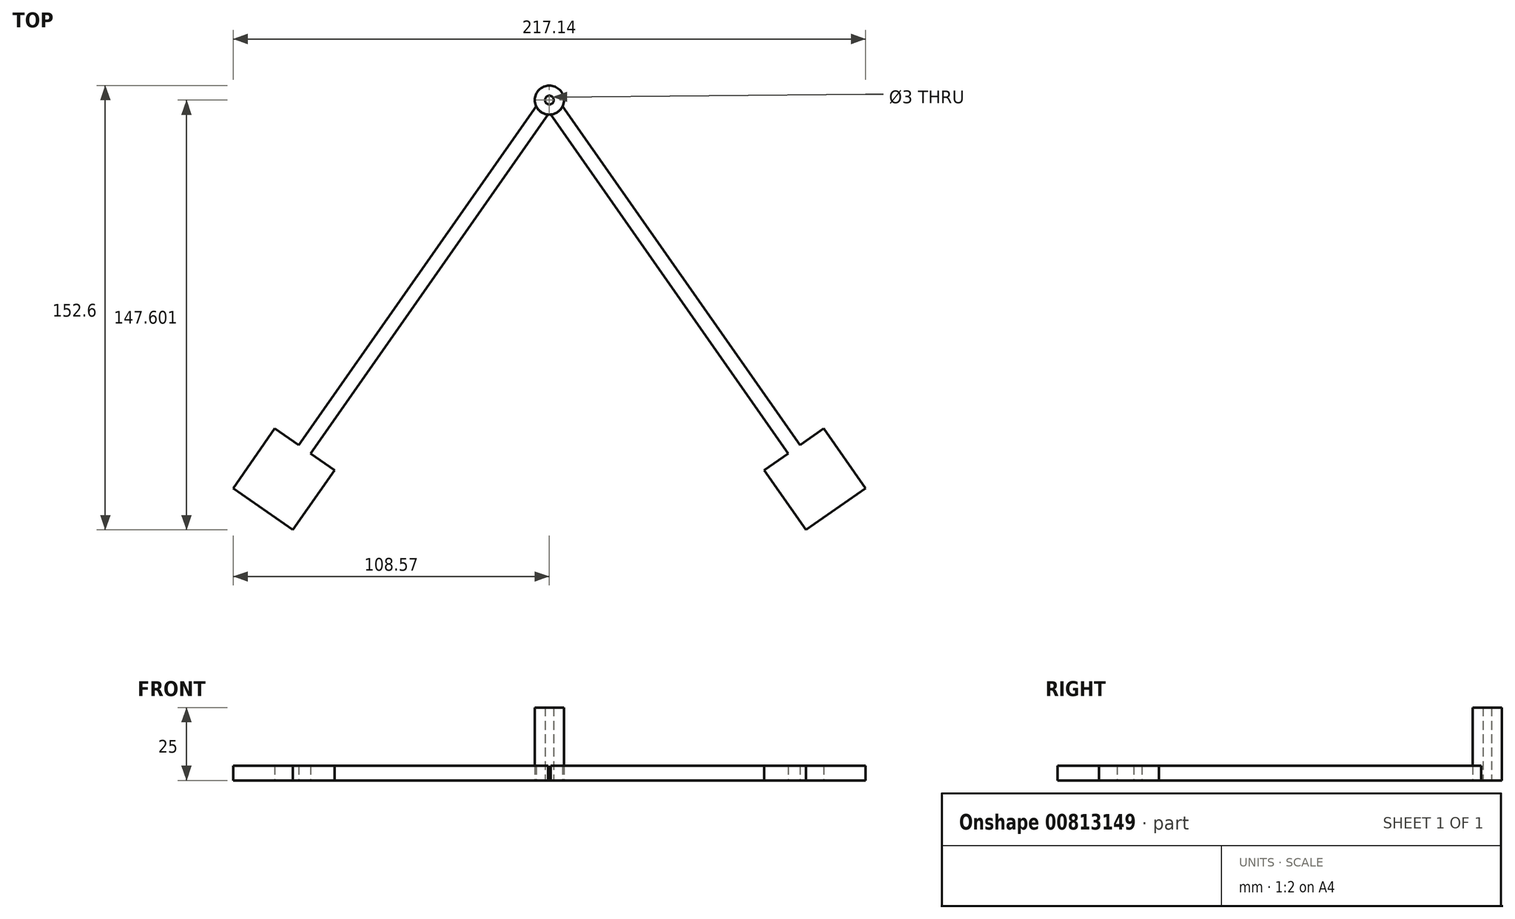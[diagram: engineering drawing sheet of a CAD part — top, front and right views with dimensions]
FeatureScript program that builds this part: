
annotation { "Feature Type Name" : "Feature", "Feature Type Description" : "" }
export const myFeature = defineFeature(function(context is Context, id is Id, definition is map)
    precondition{}
    {
        {
            var Q0;
            Q0=qCreatedBy(makeId("Top.planeOp"),FACE);
            var sketch = newSketch(context, id + "F0", { "sketchPlane" : qUnion([Q0])});
            skLineSegment(sketch, "E0", {"start": v(-94.23, -117.14) * mm, "end": v(-73.75, -131.48) * mm});
            skLineSegment(sketch, "E1", {"start": v(-73.75, -131.48) * mm, "end": v(-88.09, -151.96) * mm});
            skLineSegment(sketch, "E2", {"start": v(-88.09, -151.96) * mm, "end": v(-108.57, -137.62) * mm});
            skLineSegment(sketch, "E3", {"start": v(-108.57, -137.62) * mm, "end": v(-94.23, -117.14) * mm});
            skLineSegment(sketch, "E4", {"start": v(-0.44, -9.34) * mm, "end": v(-81.94, -125.74) * mm});
            skLineSegment(sketch, "E5", {"start": v(-4.53, -6.47) * mm, "end": v(-86.04, -122.87) * mm});
            skLineSegment(sketch, "E6.MirrorCS", {"start": v(0.44, -9.34) * mm, "end": v(81.94, -125.74) * mm});
            skLineSegment(sketch, "E7.MirrorCS", {"start": v(4.53, -6.47) * mm, "end": v(86.04, -122.87) * mm});
            skLineSegment(sketch, "E8.MirrorCS", {"start": v(94.23, -117.14) * mm, "end": v(73.75, -131.48) * mm});
            skLineSegment(sketch, "E9.MirrorCS", {"start": v(108.57, -137.62) * mm, "end": v(94.23, -117.14) * mm});
            skLineSegment(sketch, "E10.MirrorCS", {"start": v(88.09, -151.96) * mm, "end": v(108.57, -137.62) * mm});
            skLineSegment(sketch, "E11.MirrorCS", {"start": v(73.75, -131.48) * mm, "end": v(88.09, -151.96) * mm});
            skCircle(sketch, "E12", {"center": v(0, -4.36) * mm, "radius": 5 * mm});
            skCircle(sketch, "E13", {"center": v(0, -4.36) * mm, "radius": 1.5 * mm});
            skPoint(sketch, "E14.orphan", {"position": v(0, 0) * mm});
            skPoint(sketch, "E15.orphan", {"position": v(0, -8.72) * mm});
            skSolve(sketch);
        }
        {
            var Q0;
            {var subQ0=sQuery(id+"F0.wireOp",EDGE,"E4");Q0=makeQuery(id+"F0.imprint","IMPRINT",FACE,{"disambiguationData":[TD([[makeQuery(id+"F0.imprint","IMPRINT",EDGE,{"derivedFrom":subQ0}),-1.0]])]});}
            var Q1;
            {var subQ0=sQuery(id+"F0.wireOp",EDGE,"E1");Q1=makeQuery(id+"F0.imprint","IMPRINT",FACE,{"disambiguationData":[TD([[makeQuery(id+"F0.imprint","IMPRINT",EDGE,{"derivedFrom":subQ0}),-1.0]])]});}
            var Q2;
            {var subQ0=sQuery(id+"F0.wireOp",EDGE,"E6.MirrorCS");Q2=makeQuery(id+"F0.imprint","IMPRINT",FACE,{"disambiguationData":[TD([[makeQuery(id+"F0.imprint","IMPRINT",EDGE,{"derivedFrom":subQ0}),1.0]])]});}
            var Q3;
            {var subQ0=sQuery(id+"F0.wireOp",EDGE,"E9.MirrorCS");Q3=makeQuery(id+"F0.imprint","IMPRINT",FACE,{"disambiguationData":[TD([[makeQuery(id+"F0.imprint","IMPRINT",EDGE,{"derivedFrom":subQ0}),1.0]])]});}
            extrude(context, id + "F1", {"entities" : qUnion([Q0, Q1, Q2, Q3]), "depth" : 5 * mm, "offsetDistance" : 25 * mm});
        }
        {
            var Q0;
            Q0=makeQuery(id+"F0.imprint","IMPRINT",FACE,{"disambiguationData":[TD([[makeQuery(id+"F0.imprint","IMPRINT",EDGE,{"derivedFrom":sQuery(id+"F0.wireOp",EDGE,"E13")}),-1.0]])]});
            extrude(context, id + "F2", {"entities" : qUnion([Q0]), "depth" : 25 * mm, "offsetDistance" : 25 * mm});
        }
    });
